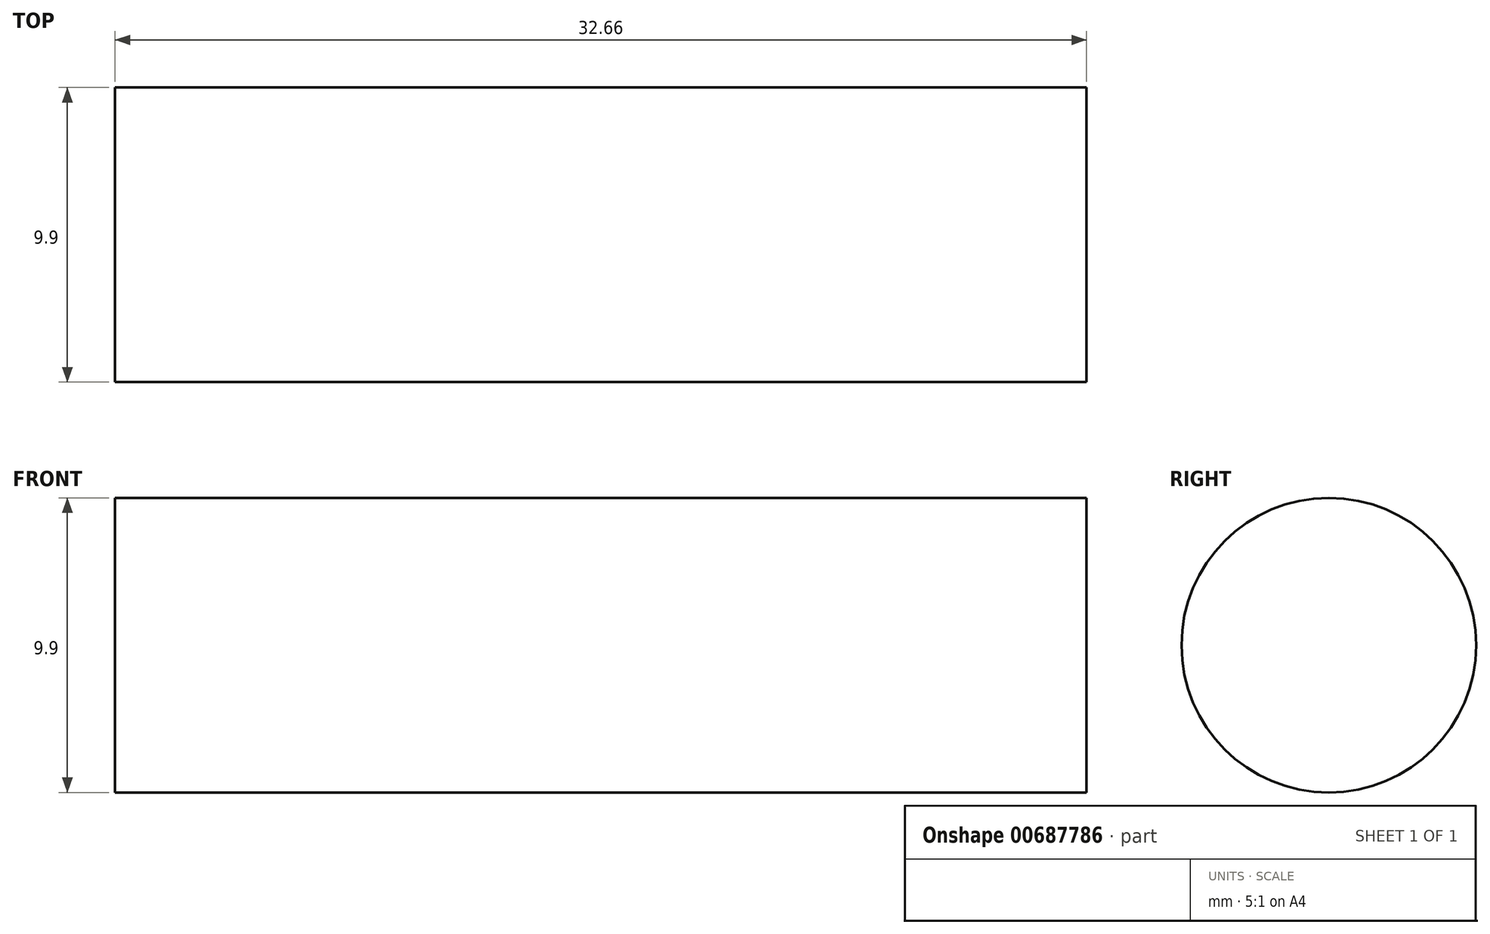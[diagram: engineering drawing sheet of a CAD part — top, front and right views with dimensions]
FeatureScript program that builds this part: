
annotation { "Feature Type Name" : "Feature", "Feature Type Description" : "" }
export const myFeature = defineFeature(function(context is Context, id is Id, definition is map)
    precondition{}
    {
        {
            var Q0;
            Q0=qCreatedBy(makeId("Right.planeOp"),FACE);
            var sketch = newSketch(context, id + "F0", { "sketchPlane" : qUnion([Q0])});
            skCircle(sketch, "E0", {"center": v(0, 0) * mm, "radius": 4.95 * mm});
            skSolve(sketch);
        }
        {
            var Q0;
            Q0=makeQuery(id+"F0.imprint","IMPRINT",FACE,{"disambiguationData":[TD([[makeQuery(id+"F0.imprint","IMPRINT",EDGE,{"derivedFrom":sQuery(id+"F0.wireOp",EDGE,"E0")}),1.0]])]});
            extrude(context, id + "F1", {"entities" : qUnion([Q0]), "depth" : 32.66 * mm, "offsetDistance" : 25.4 * mm});
        }
    });
